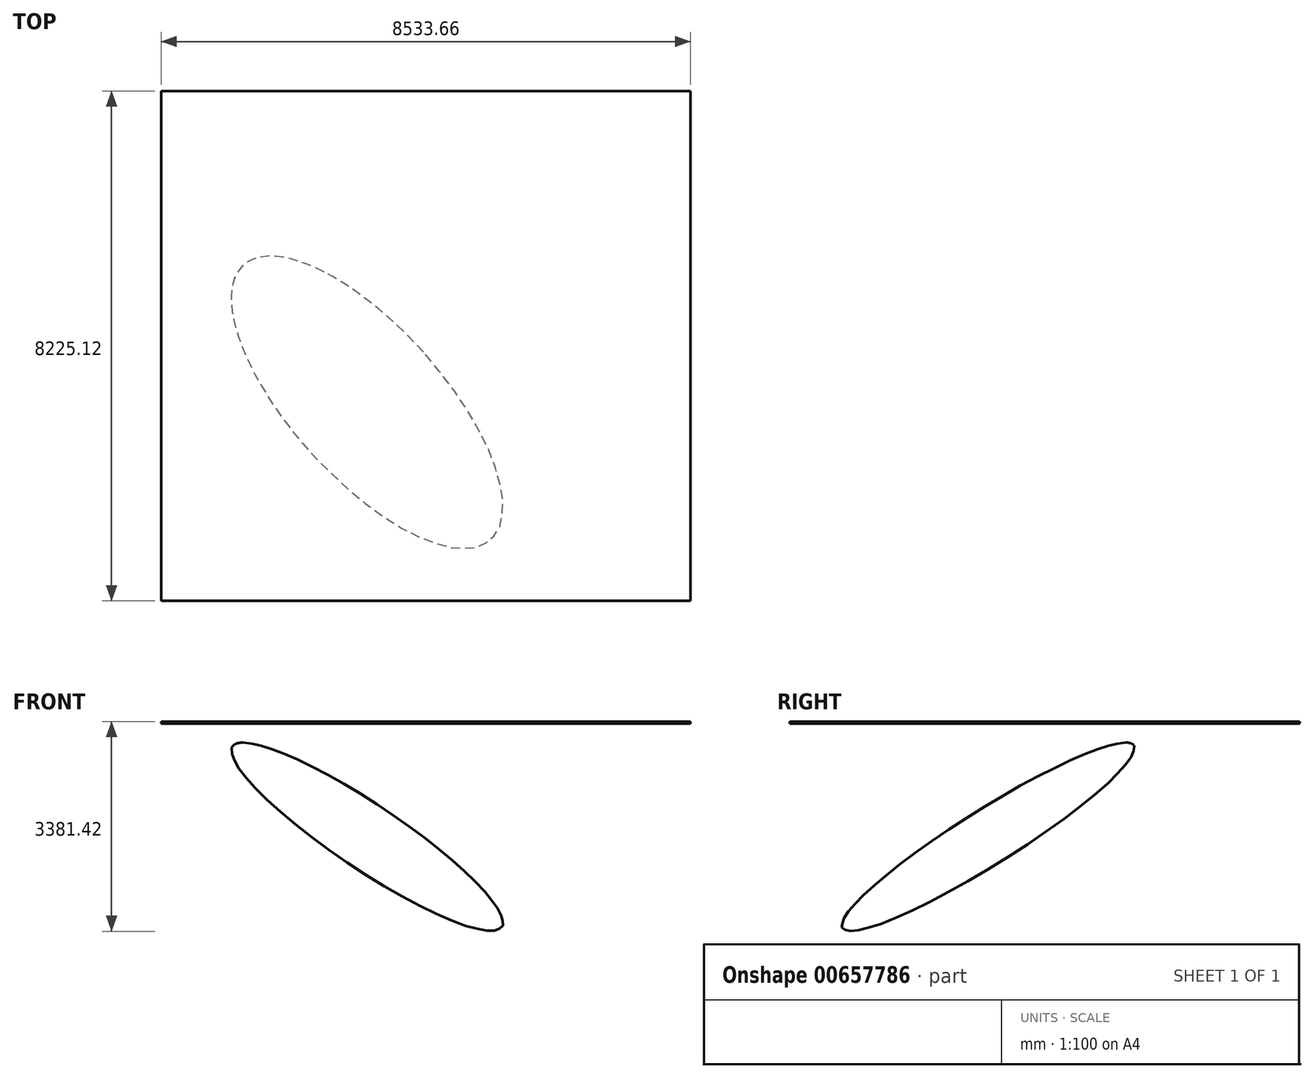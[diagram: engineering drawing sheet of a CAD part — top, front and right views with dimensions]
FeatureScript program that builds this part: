
annotation { "Feature Type Name" : "Feature", "Feature Type Description" : "" }
export const myFeature = defineFeature(function(context is Context, id is Id, definition is map)
    precondition{}
    {
        {
            assignVariable(context, id + "F0", {"name" : "Azimuth", "anyValue" : 48});
        }
        {
            assignVariable(context, id + "F1", {"name" : "Dip", "anyValue" : 27});
        }
        {
            assignVariable(context, id + "F2", {"name" : "Width", "anyValue" : .19});
        }
        {
            var Q0;
            Q0=qCreatedBy(makeId("Top.planeOp"),FACE);
            var sketch = newSketch(context, id + "F3", { "sketchPlane" : qUnion([Q0])});
            skEllipse(sketch, "E0", {"center": v(0, 0) * mm, "majorRadius": 1219.2 * mm, "minorRadius": 3352.8 * mm, "majorAxis": v(0, 1)});
            skLineSegment(sketch, "E1", {"start": v(0, 1828.8) * mm, "end": v(0, -1828.8) * mm, "construction": true});
            skLineSegment(sketch, "E2", {"start": v(-3962.4, 0) * mm, "end": v(3962.4, 0) * mm, "construction": true});
            skLineSegment(sketch, "E3.0", {"start": v(-944.88, 1219.2) * mm, "end": v(-944.88, -1219.2) * mm, "construction": true});
            skLineSegment(sketch, "E4.0", {"start": v(-3352.8, -914.4) * mm, "end": v(3352.8, -914.4) * mm, "construction": true});
            skSolve(sketch);
        }
        {
            var Q0;
            Q0=qCreatedBy(makeId("Top.planeOp"),FACE);
            var sketch = newSketch(context, id + "F4", { "sketchPlane" : qUnion([Q0])});
            skLineSegment(sketch, "E5", {"start": v(-944.88, 0) * mm, "end": v(0, 0) * mm});
            skLineSegment(sketch, "E6", {"start": v(-944.88, 0) * mm, "end": v(-944.88, -914.4) * mm});
            skSolve(sketch);
        }
        {
            var Q0;
            Q0=qSketchRegion(id+"F3",true);
            extrude(context, id + "F5", {"entities" : qUnion([Q0]), "depth" : (getVariable(context, 'Width')) * mm});
        }
        {
            var Q0;
            Q0=qCreatedBy(makeId("Front.planeOp"),FACE);
            var sketch = newSketch(context, id + "F6", { "sketchPlane" : qUnion([Q0])});
            skLineSegment(sketch, "E7", {"start": v(0, 0) * mm, "end": v(0, -1828.8) * mm, "construction": true});
            skSolve(sketch);
        }
        {
            var Q0;
            Q0=makeQuery(id+"F5.opExtrude","SWEPT_BODY",BODY,{"disambiguationData":[OSD([sQuery(id+"F3.wireOp",EDGE,"E0"),sQuery(id+"F3.wireOp",EDGE,"TMMzbr5i-4nV4-ZnMr-aG6B-IGJ66UyS6uPJ")])]});
            var Q1;
            Q1=sQuery(id+"F3.wireOp",EDGE,"E1");
            transform(context, id + "F7", {"entities" : qUnion([Q0]), "transformType" : TransformType.ROTATION, "transformAxis" : qUnion([Q1]), "angle" : (getVariable(context, 'Dip')) * degree, "oppositeDirection" : true, "makeCopy" : false});
        }
        {
            var Q0;
            Q0=makeQuery(id+"F5.opExtrude","SWEPT_BODY",BODY,{"disambiguationData":[OSD([sQuery(id+"F3.wireOp",EDGE,"E0")])]});
            var Q1;
            Q1=sQuery(id+"F6.wireOp",EDGE,"E7");
            transform(context, id + "F8", {"entities" : qUnion([Q0]), "transformType" : TransformType.ROTATION, "transformAxis" : qUnion([Q1]), "angle" : (getVariable(context, 'Azimuth')) * degree, "makeCopy" : false});
        }
        {
            var Q0;
            Q0=makeQuery(id+"F5.opExtrude","SWEPT_BODY",BODY,{"disambiguationData":[OSD([sQuery(id+"F3.wireOp",EDGE,"E0"),sQuery(id+"F3.wireOp",EDGE,"TMMzbr5i-4nV4-ZnMr-aG6B-IGJ66UyS6uPJ")])]});
            var Q1;
            Q1=sQuery(id+"F4.wireOp",EDGE,"E5");
            transform(context, id + "F9", {"entities" : qUnion([Q0]), "transformType" : TransformType.TRANSLATION_ENTITY, "oppositeDirectionEntity" : true, "transformLine" : qUnion([Q1]), "makeCopy" : false});
        }
        {
            var Q0;
            Q0=makeQuery(id+"F5.opExtrude","SWEPT_BODY",BODY,{"disambiguationData":[OSD([sQuery(id+"F3.wireOp",EDGE,"E0"),sQuery(id+"F3.wireOp",EDGE,"TMMzbr5i-4nV4-ZnMr-aG6B-IGJ66UyS6uPJ")])]});
            var Q1;
            Q1=sQuery(id+"F4.wireOp",EDGE,"E6");
            transform(context, id + "F10", {"entities" : qUnion([Q0]), "transformType" : TransformType.TRANSLATION_ENTITY, "oppositeDirectionEntity" : false, "transformLine" : qUnion([Q1]), "makeCopy" : false});
        }
        {
            var Q0;
            Q0=qCreatedBy(makeId("Top.planeOp"),FACE);
            var sketch = newSketch(context, id + "F11", { "sketchPlane" : qUnion([Q0])});
            skCircle(sketch, "E8", {"center": v(0, 0) * mm, "radius": 76.2 * mm});
            skSolve(sketch);
        }
        {
            var Q0;
            Q0=qSketchRegion(id+"F11",true);
            extrude(context, id + "F12", {"entities" : qUnion([Q0]), "operationType" : NewBodyOperationType.REMOVE, "endBound" : BoundingType.THROUGH_ALL, "oppositeDirection" : true, "depth" : 30.48 * mm, "hasSecondDirection" : true, "secondDirectionBound" : SecondDirectionBoundingType.THROUGH_ALL, "secondDirectionOppositeDirection" : false, "secondDirectionDepth" : 30.48 * mm});
        }
        {
            var Q0;
            Q0=makeQuery(id+"F5.opExtrude","SWEPT_BODY",BODY,{"disambiguationData":[OSD([sQuery(id+"F3.wireOp",EDGE,"E0")])]});
            var Q1;
            Q1=sQuery(id+"F6.wireOp",EDGE,"E7");
            transform(context, id + "F13", {"entities" : qUnion([Q0]), "transformType" : TransformType.TRANSLATION_ENTITY, "oppositeDirectionEntity" : false, "transformLine" : qUnion([Q1]), "makeCopy" : false});
        }
        {
            var Q0;
            Q0=qCreatedBy(makeId("Top.planeOp"),FACE);
            var sketch = newSketch(context, id + "F14", { "sketchPlane" : qUnion([Q0])});
            skLineSegment(sketch, "E9.bottom", {"start": v(-4266.83, -4112.56) * mm, "end": v(4266.83, -4112.56) * mm});
            skLineSegment(sketch, "E9.top", {"start": v(-4266.83, 4112.56) * mm, "end": v(4266.83, 4112.56) * mm});
            skLineSegment(sketch, "E9.left", {"start": v(-4266.83, -4112.56) * mm, "end": v(-4266.83, 4112.56) * mm});
            skLineSegment(sketch, "E9.right", {"start": v(4266.83, -4112.56) * mm, "end": v(4266.83, 4112.56) * mm});
            skPoint(sketch, "E9.middle", {"position": v(0, 0) * mm});
            skSolve(sketch);
        }
        {
            var Q0;
            Q0=makeQuery(id+"F14.imprint","IMPRINT",FACE,{"disambiguationData":[TD([[makeQuery(id+"F14.imprint","IMPRINT",EDGE,{"derivedFrom":sQuery(id+"F14.wireOp",EDGE,"E9.bottom")}),1.0]])]});
            extrude(context, id + "F15", {"entities" : qUnion([Q0]), "depth" : 30.48 * mm});
        }
    });
